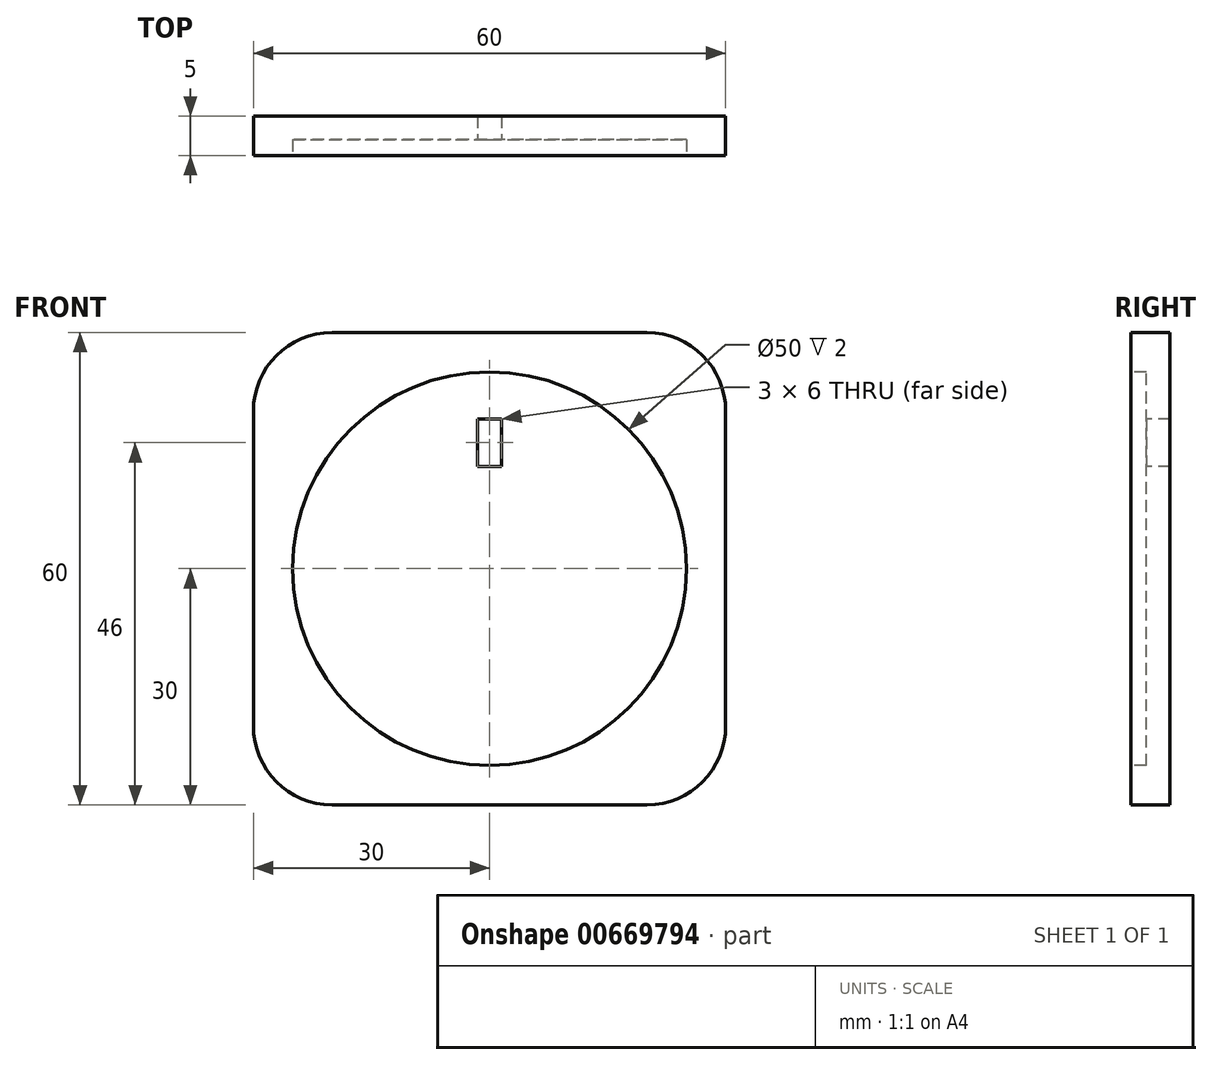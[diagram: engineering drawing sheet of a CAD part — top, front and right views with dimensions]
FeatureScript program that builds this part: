
annotation { "Feature Type Name" : "Feature", "Feature Type Description" : "" }
export const myFeature = defineFeature(function(context is Context, id is Id, definition is map)
    precondition{}
    {
        {
            var Q0;
            Q0=qCreatedBy(makeId("Front.planeOp"),FACE);
            var sketch = newSketch(context, id + "F0", { "sketchPlane" : qUnion([Q0]), "disableImprinting" : false});
            skLineSegment(sketch, "E0.bottom", {"start": v(30, 30) * mm, "end": v(-30, 30) * mm});
            skLineSegment(sketch, "E0.top", {"start": v(30, -30) * mm, "end": v(-30, -30) * mm});
            skLineSegment(sketch, "E0.left", {"start": v(30, 30) * mm, "end": v(30, -30) * mm});
            skLineSegment(sketch, "E0.right", {"start": v(-30, 30) * mm, "end": v(-30, -30) * mm});
            skPoint(sketch, "E0.middle", {"position": v(0, 0) * mm});
            skSolve(sketch);
        }
        {
            var Q0;
            Q0 = qSketchRegion(id + "F0", true);
            extrude(context, id + "F1", {"entities" : qUnion([Q0]), "depth" : 5 * mm, "offsetDistance" : 25 * mm});
        }
        {
            var Q0;
            Q0=makeQuery(id+"F1.opExtrude","CAP_FACE",FACE,{"disambiguationData":[OSD([sQuery(id+"F0.wireOp",EDGE,"E0.bottom"),sQuery(id+"F0.wireOp",EDGE,"E0.top"),sQuery(id+"F0.wireOp",EDGE,"E0.left"),sQuery(id+"F0.wireOp",EDGE,"E0.right")])],"isStart":false});
            var sketch = newSketch(context, id + "F2", { "sketchPlane" : qUnion([Q0])});
            skCircle(sketch, "E1", {"center": v(0, 0) * mm, "radius": 25 * mm});
            skSolve(sketch);
        }
        {
            var Q0;
            Q0 = qSketchRegion(id + "F2", true);
            extrude(context, id + "F3", {"entities" : qUnion([Q0]), "operationType" : NewBodyOperationType.REMOVE, "oppositeDirection" : true, "depth" : 2 * mm, "offsetDistance" : 25 * mm});
        }
        {
            var Q0;
            Q0=makeQuery(id+"F1.opExtrude","SWEPT_EDGE",EDGE,{"disambiguationData":[OSD([sQuery(id+"F0.wireOp",EDGE,"E0.bottom"),sQuery(id+"F0.wireOp",EDGE,"E0.right")])]});
            fillet(context, id + "F4", {"entities" : qUnion([Q0]), "radius" : 10 * mm, "tangentPropagation" : true, "allowEdgeOverflow" : false});
        }
        {
            var Q0;
            Q0=makeQuery(id+"F1.opExtrude","SWEPT_EDGE",EDGE,{"disambiguationData":[OSD([sQuery(id+"F0.wireOp",EDGE,"E0.bottom"),sQuery(id+"F0.wireOp",EDGE,"E0.left")])]});
            fillet(context, id + "F5", {"entities" : qUnion([Q0]), "radius" : 10 * mm, "tangentPropagation" : true, "allowEdgeOverflow" : false});
        }
        {
            var Q0;
            Q0=makeQuery(id+"F1.opExtrude","SWEPT_EDGE",EDGE,{"disambiguationData":[OSD([sQuery(id+"F0.wireOp",EDGE,"E0.top"),sQuery(id+"F0.wireOp",EDGE,"E0.right")])]});
            fillet(context, id + "F6", {"entities" : qUnion([Q0]), "radius" : 10 * mm, "tangentPropagation" : true, "allowEdgeOverflow" : false});
        }
        {
            var Q0;
            Q0=makeQuery(id+"F1.opExtrude","SWEPT_EDGE",EDGE,{"disambiguationData":[OSD([sQuery(id+"F0.wireOp",EDGE,"E0.top"),sQuery(id+"F0.wireOp",EDGE,"E0.left")])]});
            fillet(context, id + "F7", {"entities" : qUnion([Q0]), "radius" : 10 * mm, "tangentPropagation" : true, "allowEdgeOverflow" : false});
        }
        {
            var Q0;
            Q0=makeQuery(id+"F3.boolean.opBoolean","COPY",FACE,{"derivedFrom":makeQuery(id+"F3.opExtrude","CAP_FACE",FACE,{"disambiguationData":[OSD([sQuery(id+"F2.wireOp",EDGE,"E1")])],"isStart":false})});
            var sketch = newSketch(context, id + "F8", { "sketchPlane" : qUnion([Q0]), "disableImprinting" : false});
            skLineSegment(sketch, "E2.bottom", {"start": v(-1.5, 19) * mm, "end": v(1.5, 19) * mm});
            skLineSegment(sketch, "E2.top", {"start": v(-1.5, 13) * mm, "end": v(1.5, 13) * mm});
            skLineSegment(sketch, "E2.left", {"start": v(-1.5, 19) * mm, "end": v(-1.5, 13) * mm});
            skLineSegment(sketch, "E2.right", {"start": v(1.5, 19) * mm, "end": v(1.5, 13) * mm});
            skSolve(sketch);
        }
        {
            var Q0;
            Q0=makeQuery(id+"F8.imprint","IMPRINT",FACE,{"disambiguationData":[TD([[makeQuery(id+"F8.imprint","IMPRINT",EDGE,{"derivedFrom":sQuery(id+"F8.wireOp",EDGE,"E2.bottom")}),-1.0]])]});
            extrude(context, id + "F9", {"entities" : qUnion([Q0]), "operationType" : NewBodyOperationType.REMOVE, "endBound" : BoundingType.THROUGH_ALL, "oppositeDirection" : true, "depth" : 25 * mm, "offsetDistance" : 25 * mm});
        }
    });
